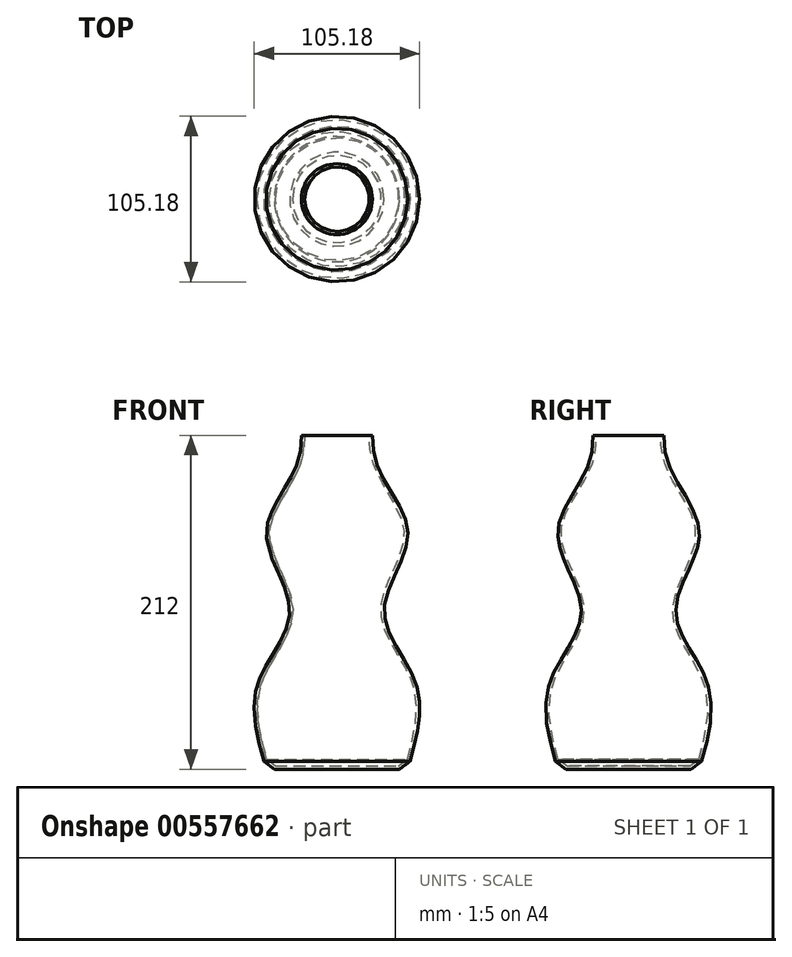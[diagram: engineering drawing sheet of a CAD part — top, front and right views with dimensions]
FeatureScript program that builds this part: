
annotation { "Feature Type Name" : "Feature", "Feature Type Description" : "" }
export const myFeature = defineFeature(function(context is Context, id is Id, definition is map)
    precondition{}
    {
        {
            var Q0;
            Q0=qCreatedBy(makeId("Top.planeOp"),FACE);
            var sketch = newSketch(context, id + "F0", { "sketchPlane" : qUnion([Q0])});
            skCircle(sketch, "E0", {"center": v(0, 0) * mm, "radius": 22.5 * mm});
            skSolve(sketch);
        }
        {
            var Q0;
            Q0=qCreatedBy(makeId("Top.planeOp"),FACE);
            cPlane(context, id + "F1", {"entities" : qUnion([Q0]), "cplaneType" : CPlaneType.OFFSET, "offset" : 12 * mm, "oppositeDirection" : true, "width" : 150 * mm, "height" : 150 * mm});
        }
        {
            var Q0;
            Q0=qCreatedBy(id+"F1.planeOp",FACE);
            var sketch = newSketch(context, id + "F2", { "sketchPlane" : qUnion([Q0])});
            skCircle(sketch, "E1", {"center": v(0, 0) * mm, "radius": 23.5 * mm});
            skSolve(sketch);
        }
        {
            var Q0;
            Q0=qCreatedBy(id+"F1.planeOp",FACE);
            cPlane(context, id + "F3", {"entities" : qUnion([Q0]), "cplaneType" : CPlaneType.OFFSET, "offset" : 50 * mm, "oppositeDirection" : true, "width" : 150 * mm, "height" : 150 * mm});
        }
        {
            var Q0;
            Q0=qCreatedBy(id+"F3.planeOp",FACE);
            cPlane(context, id + "F4", {"entities" : qUnion([Q0]), "cplaneType" : CPlaneType.OFFSET, "offset" : 150 * mm, "oppositeDirection" : true, "width" : 150 * mm, "height" : 150 * mm});
        }
        {
            var Q0;
            Q0=qCreatedBy(id+"F3.planeOp",FACE);
            cPlane(context, id + "F5", {"entities" : qUnion([Q0]), "cplaneType" : CPlaneType.OFFSET, "offset" : 50 * mm, "oppositeDirection" : true, "width" : 150 * mm, "height" : 150 * mm});
        }
        {
            var Q0;
            Q0=qCreatedBy(id+"F3.planeOp",FACE);
            var sketch = newSketch(context, id + "F6", { "sketchPlane" : qUnion([Q0])});
            skCircle(sketch, "E2", {"center": v(0, 0) * mm, "radius": 45 * mm});
            skSolve(sketch);
        }
        {
            var Q0;
            Q0=qCreatedBy(id+"F4.planeOp",FACE);
            var sketch = newSketch(context, id + "F7", { "sketchPlane" : qUnion([Q0])});
            skCircle(sketch, "E3", {"center": v(0, 0) * mm, "radius": 45 * mm});
            skSolve(sketch);
        }
        {
            var Q0;
            Q0=qCreatedBy(id+"F5.planeOp",FACE);
            var sketch = newSketch(context, id + "F8", { "sketchPlane" : qUnion([Q0])});
            skCircle(sketch, "E4", {"center": v(0, 0) * mm, "radius": 30 * mm});
            skSolve(sketch);
        }
        {
            var Q0;
            Q0=qCreatedBy(id+"F5.planeOp",FACE);
            cPlane(context, id + "F9", {"entities" : qUnion([Q0]), "cplaneType" : CPlaneType.OFFSET, "offset" : 45 * mm, "oppositeDirection" : true, "width" : 150 * mm, "height" : 150 * mm});
        }
        {
            var Q0;
            Q0=qCreatedBy(id+"F9.planeOp",FACE);
            var sketch = newSketch(context, id + "F10", { "sketchPlane" : qUnion([Q0])});
            skCircle(sketch, "E5", {"center": v(0, 0) * mm, "radius": 50 * mm});
            skSolve(sketch);
        }
        {
            var Q0;
            Q0=makeQuery(id+"F7.imprint","IMPRINT",FACE,{"disambiguationData":[TD([[makeQuery(id+"F7.imprint","IMPRINT",EDGE,{"derivedFrom":sQuery(id+"F7.wireOp",EDGE,"E3")}),1.0]])]});
            var Q1;
            Q1=makeQuery(id+"F10.imprint","IMPRINT",FACE,{"disambiguationData":[TD([[makeQuery(id+"F10.imprint","IMPRINT",EDGE,{"derivedFrom":sQuery(id+"F10.wireOp",EDGE,"E5")}),1.0]])]});
            var Q2;
            Q2=makeQuery(id+"F8.imprint","IMPRINT",FACE,{"disambiguationData":[TD([[makeQuery(id+"F8.imprint","IMPRINT",EDGE,{"derivedFrom":sQuery(id+"F8.wireOp",EDGE,"E4")}),1.0]])]});
            var Q3;
            Q3=makeQuery(id+"F6.imprint","IMPRINT",FACE,{"disambiguationData":[TD([[makeQuery(id+"F6.imprint","IMPRINT",EDGE,{"derivedFrom":sQuery(id+"F6.wireOp",EDGE,"E2")}),1.0]])]});
            var Q4;
            Q4=makeQuery(id+"F2.imprint","IMPRINT",FACE,{"disambiguationData":[TD([[makeQuery(id+"F2.imprint","IMPRINT",EDGE,{"derivedFrom":sQuery(id+"F2.wireOp",EDGE,"E1")}),1.0]])]});
            var Q5;
            Q5=makeQuery(id+"F0.imprint","IMPRINT",FACE,{"disambiguationData":[TD([[makeQuery(id+"F0.imprint","IMPRINT",EDGE,{"derivedFrom":sQuery(id+"F0.wireOp",EDGE,"E0")}),1.0]])]});
            loft(context, id + "F11", {"sheetProfilesArray" : [{ "sheetProfileEntities" : qUnion([Q0]) }, { "sheetProfileEntities" : qUnion([Q1]) }, { "sheetProfileEntities" : qUnion([Q2]) }, { "sheetProfileEntities" : qUnion([Q3]) }, { "sheetProfileEntities" : qUnion([Q4]) }, { "sheetProfileEntities" : qUnion([Q5]) }]});
        }
        {
            var Q0;
            Q0=makeQuery(id+"F11.opLoft","MID_CAP_EDGE",EDGE,{"disambiguationData":[OSD([sQuery(id+"F7.wireOp",EDGE,"E3")])],"capPos":0.0});
            chamfer(context, id + "F12", {"entities" : qUnion([Q0]), "width" : 7 * mm, "tangentPropagation" : true});
        }
        {
            var Q0;
            Q0=makeQuery(id+"F11.opLoft","CAP_FACE",FACE,{"disambiguationData":[OSD([makeQuery(id+"F0.imprint","IMPRINT",FACE,{"disambiguationData":[TD([[makeQuery(id+"F0.imprint","IMPRINT",EDGE,{"derivedFrom":sQuery(id+"F0.wireOp",EDGE,"E0")}),1.0]])]})])],"isStart":true});
            shell(context, id + "F13", {"entities" : qUnion([Q0]), "thickness" : 2 * mm});
        }
    });
